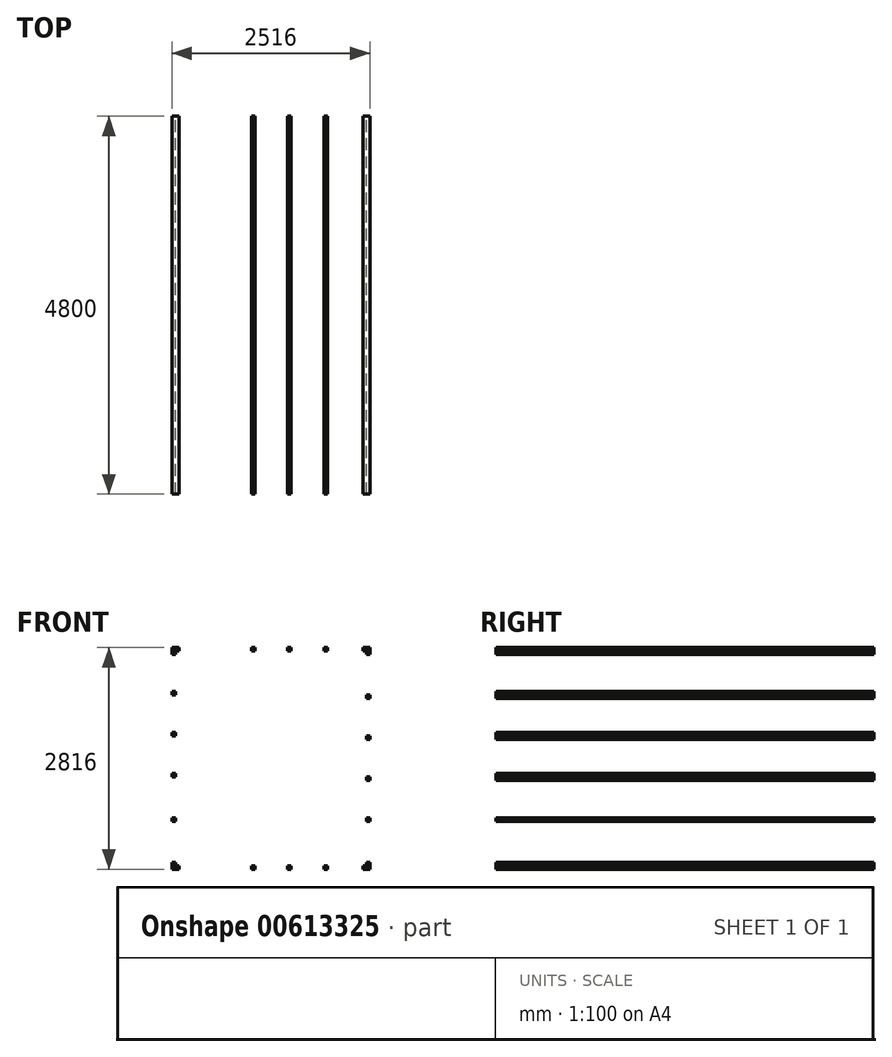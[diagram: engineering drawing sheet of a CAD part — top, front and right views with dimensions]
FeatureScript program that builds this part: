
annotation { "Feature Type Name" : "Feature", "Feature Type Description" : "" }
export const myFeature = defineFeature(function(context is Context, id is Id, definition is map)
    precondition{}
    {
        {
            var Q0;
            Q0=qCreatedBy(makeId("Front.planeOp"),FACE);
            var sketch = newSketch(context, id + "F0", { "sketchPlane" : qUnion([Q0])});
            skLineSegment(sketch, "E0.bottom", {"start": v(0, 0) * mm, "end": v(2400, 0) * mm});
            skLineSegment(sketch, "E0.top", {"start": v(0, 2700) * mm, "end": v(2400, 2700) * mm});
            skLineSegment(sketch, "E0.left", {"start": v(0, 0) * mm, "end": v(0, 2700) * mm});
            skLineSegment(sketch, "E0.right", {"start": v(2400, 0) * mm, "end": v(2400, 2700) * mm});
            skLineSegment(sketch, "E1.0", {"start": v(145, 2555) * mm, "end": v(2255, 2555) * mm});
            skLineSegment(sketch, "E1.1", {"start": v(145, 145) * mm, "end": v(145, 2555) * mm});
            skLineSegment(sketch, "E1.2", {"start": v(145, 145) * mm, "end": v(2255, 145) * mm});
            skLineSegment(sketch, "E1.3", {"start": v(2255, 145) * mm, "end": v(2255, 2555) * mm});
            skLineSegment(sketch, "E2.0", {"start": v(-13, 2713) * mm, "end": v(2413, 2713) * mm});
            skLineSegment(sketch, "E2.1", {"start": v(-13, -13) * mm, "end": v(-13, 2713) * mm});
            skLineSegment(sketch, "E2.2", {"start": v(-13, -13) * mm, "end": v(2413, -13) * mm});
            skLineSegment(sketch, "E2.3", {"start": v(2413, -13) * mm, "end": v(2413, 2713) * mm});
            skLineSegment(sketch, "E3.bottom", {"start": v(-13, 2713) * mm, "end": v(-58, 2713) * mm});
            skLineSegment(sketch, "E3.top", {"start": v(-13, 2668) * mm, "end": v(-58, 2668) * mm});
            skLineSegment(sketch, "E3.left", {"start": v(-13, 2713) * mm, "end": v(-13, 2668) * mm});
            skLineSegment(sketch, "E3.right", {"start": v(-58, 2713) * mm, "end": v(-58, 2668) * mm});
            skLineSegment(sketch, "E4.bottom", {"start": v(2413, 2713) * mm, "end": v(2458, 2713) * mm});
            skLineSegment(sketch, "E4.top", {"start": v(2413, 2668) * mm, "end": v(2458, 2668) * mm});
            skLineSegment(sketch, "E4.left", {"start": v(2413, 2713) * mm, "end": v(2413, 2668) * mm});
            skLineSegment(sketch, "E4.right", {"start": v(2458, 2713) * mm, "end": v(2458, 2668) * mm});
            skLineSegment(sketch, "E5.bottom", {"start": v(-13, -13) * mm, "end": v(-58, -13) * mm});
            skLineSegment(sketch, "E5.top", {"start": v(-13, 32) * mm, "end": v(-58, 32) * mm});
            skLineSegment(sketch, "E5.left", {"start": v(-13, -13) * mm, "end": v(-13, 32) * mm});
            skLineSegment(sketch, "E5.right", {"start": v(-58, -13) * mm, "end": v(-58, 32) * mm});
            skLineSegment(sketch, "E6.bottom", {"start": v(2413, -13) * mm, "end": v(2458, -13) * mm});
            skLineSegment(sketch, "E6.top", {"start": v(2413, 32) * mm, "end": v(2458, 32) * mm});
            skLineSegment(sketch, "E6.left", {"start": v(2413, -13) * mm, "end": v(2413, 32) * mm});
            skLineSegment(sketch, "E6.right", {"start": v(2458, -13) * mm, "end": v(2458, 32) * mm});
            skLineSegment(sketch, "E7.bottom", {"start": v(-58, 2713) * mm, "end": v(32, 2713) * mm});
            skLineSegment(sketch, "E7.top", {"start": v(-58, 2758) * mm, "end": v(32, 2758) * mm});
            skLineSegment(sketch, "E7.left", {"start": v(-58, 2713) * mm, "end": v(-58, 2758) * mm});
            skLineSegment(sketch, "E7.right", {"start": v(32, 2713) * mm, "end": v(32, 2758) * mm});
            skLineSegment(sketch, "E8.bottom", {"start": v(-58, -13) * mm, "end": v(32, -13) * mm});
            skLineSegment(sketch, "E8.top", {"start": v(-58, -58) * mm, "end": v(32, -58) * mm});
            skLineSegment(sketch, "E8.left", {"start": v(-58, -13) * mm, "end": v(-58, -58) * mm});
            skLineSegment(sketch, "E8.right", {"start": v(32, -13) * mm, "end": v(32, -58) * mm});
            skLineSegment(sketch, "E9.bottom", {"start": v(2458, -13) * mm, "end": v(2368, -13) * mm});
            skLineSegment(sketch, "E9.top", {"start": v(2458, -58) * mm, "end": v(2368, -58) * mm});
            skLineSegment(sketch, "E9.left", {"start": v(2458, -13) * mm, "end": v(2458, -58) * mm});
            skLineSegment(sketch, "E9.right", {"start": v(2368, -13) * mm, "end": v(2368, -58) * mm});
            skLineSegment(sketch, "E10.bottom", {"start": v(2458, 2713) * mm, "end": v(2368, 2713) * mm});
            skLineSegment(sketch, "E10.top", {"start": v(2458, 2758) * mm, "end": v(2368, 2758) * mm});
            skLineSegment(sketch, "E10.left", {"start": v(2458, 2713) * mm, "end": v(2458, 2758) * mm});
            skLineSegment(sketch, "E10.right", {"start": v(2368, 2713) * mm, "end": v(2368, 2758) * mm});
            skLineSegment(sketch, "E11.bottom", {"start": v(492, 2713) * mm, "end": v(537, 2713) * mm});
            skLineSegment(sketch, "E11.top", {"start": v(492, 2758) * mm, "end": v(537, 2758) * mm});
            skLineSegment(sketch, "E11.left", {"start": v(492, 2713) * mm, "end": v(492, 2758) * mm});
            skLineSegment(sketch, "E11.right", {"start": v(537, 2713) * mm, "end": v(537, 2758) * mm});
            skLineSegment(sketch, "E12.1.0.0", {"start": v(952, 2713) * mm, "end": v(952, 2758) * mm});
            skLineSegment(sketch, "E12.1.0.1", {"start": v(952, 2758) * mm, "end": v(997, 2758) * mm});
            skLineSegment(sketch, "E12.1.0.2", {"start": v(997, 2713) * mm, "end": v(997, 2758) * mm});
            skLineSegment(sketch, "E12.2.0.0", {"start": v(1412, 2713) * mm, "end": v(1412, 2758) * mm});
            skLineSegment(sketch, "E12.2.0.1", {"start": v(1412, 2758) * mm, "end": v(1457, 2758) * mm});
            skLineSegment(sketch, "E12.2.0.2", {"start": v(1457, 2713) * mm, "end": v(1457, 2758) * mm});
            skLineSegment(sketch, "E12.3.0.0", {"start": v(1872, 2713) * mm, "end": v(1872, 2758) * mm});
            skLineSegment(sketch, "E12.3.0.1", {"start": v(1872, 2758) * mm, "end": v(1917, 2758) * mm});
            skLineSegment(sketch, "E12.3.0.2", {"start": v(1917, 2713) * mm, "end": v(1917, 2758) * mm});
            skLineSegment(sketch, "E12.direction1", {"start": v(492, 2713) * mm, "end": v(952, 2713) * mm, "construction": true});
            skLineSegment(sketch, "E13.bottom", {"start": v(492, -13) * mm, "end": v(537, -13) * mm});
            skLineSegment(sketch, "E13.top", {"start": v(492, -58) * mm, "end": v(537, -58) * mm});
            skLineSegment(sketch, "E13.left", {"start": v(492, -13) * mm, "end": v(492, -58) * mm});
            skLineSegment(sketch, "E13.right", {"start": v(537, -13) * mm, "end": v(537, -58) * mm});
            skLineSegment(sketch, "E14.1.0.0", {"start": v(952, -13) * mm, "end": v(952, -58) * mm});
            skLineSegment(sketch, "E14.1.0.1", {"start": v(952, -58) * mm, "end": v(997, -58) * mm});
            skLineSegment(sketch, "E14.1.0.2", {"start": v(997, -13) * mm, "end": v(997, -58) * mm});
            skLineSegment(sketch, "E14.2.0.0", {"start": v(1412, -13) * mm, "end": v(1412, -58) * mm});
            skLineSegment(sketch, "E14.2.0.1", {"start": v(1412, -58) * mm, "end": v(1457, -58) * mm});
            skLineSegment(sketch, "E14.2.0.2", {"start": v(1457, -13) * mm, "end": v(1457, -58) * mm});
            skLineSegment(sketch, "E14.3.0.0", {"start": v(1872, -13) * mm, "end": v(1872, -58) * mm});
            skLineSegment(sketch, "E14.3.0.1", {"start": v(1872, -58) * mm, "end": v(1917, -58) * mm});
            skLineSegment(sketch, "E14.3.0.2", {"start": v(1917, -13) * mm, "end": v(1917, -58) * mm});
            skLineSegment(sketch, "E14.direction1", {"start": v(492, -58) * mm, "end": v(952, -58) * mm, "construction": true});
            skLineSegment(sketch, "E15.bottom", {"start": v(-13, 597) * mm, "end": v(-58, 597) * mm});
            skLineSegment(sketch, "E15.top", {"start": v(-13, 552) * mm, "end": v(-58, 552) * mm});
            skLineSegment(sketch, "E15.left", {"start": v(-13, 597) * mm, "end": v(-13, 552) * mm});
            skLineSegment(sketch, "E15.right", {"start": v(-58, 597) * mm, "end": v(-58, 552) * mm});
            skLineSegment(sketch, "E16.bottom", {"start": v(2413, 597) * mm, "end": v(2458, 597) * mm});
            skLineSegment(sketch, "E16.top", {"start": v(2413, 552) * mm, "end": v(2458, 552) * mm});
            skLineSegment(sketch, "E16.left", {"start": v(2413, 597) * mm, "end": v(2413, 552) * mm});
            skLineSegment(sketch, "E16.right", {"start": v(2458, 597) * mm, "end": v(2458, 552) * mm});
            skLineSegment(sketch, "E17.0.1.0", {"start": v(2413, 1117) * mm, "end": v(2458, 1117) * mm});
            skLineSegment(sketch, "E17.0.1.1", {"start": v(2413, 1072) * mm, "end": v(2458, 1072) * mm});
            skLineSegment(sketch, "E17.0.1.2", {"start": v(2458, 1117) * mm, "end": v(2458, 1072) * mm});
            skLineSegment(sketch, "E17.0.2.0", {"start": v(2413, 1637) * mm, "end": v(2458, 1637) * mm});
            skLineSegment(sketch, "E17.0.2.1", {"start": v(2413, 1592) * mm, "end": v(2458, 1592) * mm});
            skLineSegment(sketch, "E17.0.2.2", {"start": v(2458, 1637) * mm, "end": v(2458, 1592) * mm});
            skLineSegment(sketch, "E17.0.3.0", {"start": v(2413, 2157) * mm, "end": v(2458, 2157) * mm});
            skLineSegment(sketch, "E17.0.3.1", {"start": v(2413, 2112) * mm, "end": v(2458, 2112) * mm});
            skLineSegment(sketch, "E17.0.3.2", {"start": v(2458, 2157) * mm, "end": v(2458, 2112) * mm});
            skLineSegment(sketch, "E17.direction1", {"start": v(2413, 552) * mm, "end": v(2438, 552) * mm, "construction": true});
            skLineSegment(sketch, "E17.direction2", {"start": v(2413, 552) * mm, "end": v(2413, 1072) * mm, "construction": true});
            skLineSegment(sketch, "E18.bottom", {"start": v(-13, 1117) * mm, "end": v(-58, 1117) * mm});
            skLineSegment(sketch, "E18.top", {"start": v(-13, 1162) * mm, "end": v(-58, 1162) * mm});
            skLineSegment(sketch, "E18.left", {"start": v(-13, 1117) * mm, "end": v(-13, 1162) * mm});
            skLineSegment(sketch, "E18.right", {"start": v(-58, 1117) * mm, "end": v(-58, 1162) * mm});
            skLineSegment(sketch, "E19.0.1.0", {"start": v(-13, 1682) * mm, "end": v(-58, 1682) * mm});
            skLineSegment(sketch, "E19.0.1.1", {"start": v(-58, 1637) * mm, "end": v(-58, 1682) * mm});
            skLineSegment(sketch, "E19.0.1.2", {"start": v(-13, 1637) * mm, "end": v(-58, 1637) * mm});
            skLineSegment(sketch, "E19.0.2.0", {"start": v(-13, 2202) * mm, "end": v(-58, 2202) * mm});
            skLineSegment(sketch, "E19.0.2.1", {"start": v(-58, 2157) * mm, "end": v(-58, 2202) * mm});
            skLineSegment(sketch, "E19.0.2.2", {"start": v(-13, 2157) * mm, "end": v(-58, 2157) * mm});
            skLineSegment(sketch, "E19.direction1", {"start": v(-58, 1117) * mm, "end": v(-33, 1117) * mm, "construction": true});
            skLineSegment(sketch, "E19.direction2", {"start": v(-58, 1117) * mm, "end": v(-58, 1637) * mm, "construction": true});
            skLineSegment(sketch, "E20.0", {"start": v(-58, 2758) * mm, "end": v(2458, 2758) * mm});
            skLineSegment(sketch, "E20.1", {"start": v(-58, -58) * mm, "end": v(-58, 2758) * mm});
            skLineSegment(sketch, "E20.2", {"start": v(-58, -58) * mm, "end": v(2458, -58) * mm});
            skLineSegment(sketch, "E20.3", {"start": v(2458, -58) * mm, "end": v(2458, 2758) * mm});
            skSolve(sketch);
        }
        {
            var Q0;
            Q0=makeQuery(id+"F0.imprint","IMPRINT",FACE,{"disambiguationData":[TD([[makeQuery(id+"F0.imprint","IMPRINT",EDGE,{"derivedFrom":sQuery(id+"F0.wireOp",EDGE,"E7.top")}),-1.0]])]});
            var Q1;
            Q1=makeQuery(id+"F0.imprint","IMPRINT",FACE,{"disambiguationData":[TD([[makeQuery(id+"F0.imprint","IMPRINT",EDGE,{"derivedFrom":sQuery(id+"F0.wireOp",EDGE,"E10.top")}),1.0]])]});
            var Q2;
            Q2=makeQuery(id+"F0.imprint","IMPRINT",FACE,{"disambiguationData":[TD([[makeQuery(id+"F0.imprint","IMPRINT",EDGE,{"derivedFrom":sQuery(id+"F0.wireOp",EDGE,"E8.top")}),1.0]])]});
            var Q3;
            Q3=makeQuery(id+"F0.imprint","IMPRINT",FACE,{"disambiguationData":[TD([[makeQuery(id+"F0.imprint","IMPRINT",EDGE,{"derivedFrom":sQuery(id+"F0.wireOp",EDGE,"E9.top")}),-1.0]])]});
            extrude(context, id + "F1", {"entities" : qUnion([Q0, Q1, Q2, Q3]), "depth" : 4800 * mm, "offsetDistance" : 25 * mm});
        }
        {
            var Q0;
            Q0=makeQuery(id+"F0.imprint","IMPRINT",FACE,{"disambiguationData":[TD([[makeQuery(id+"F0.imprint","IMPRINT",EDGE,{"derivedFrom":sQuery(id+"F0.wireOp",EDGE,"E3.top")}),-1.0]])]});
            var Q1;
            Q1=makeQuery(id+"F0.imprint","IMPRINT",FACE,{"disambiguationData":[TD([[makeQuery(id+"F0.imprint","IMPRINT",EDGE,{"derivedFrom":sQuery(id+"F0.wireOp",EDGE,"E4.top")}),1.0]])]});
            var Q2;
            Q2=makeQuery(id+"F0.imprint","IMPRINT",FACE,{"disambiguationData":[TD([[makeQuery(id+"F0.imprint","IMPRINT",EDGE,{"derivedFrom":sQuery(id+"F0.wireOp",EDGE,"E11.bottom")}),1.0]])]});
            var Q3;
            {var subQ0=sQuery(id+"F0.wireOp",EDGE,"E12.1.0.0");Q3=makeQuery(id+"F0.imprint","IMPRINT",FACE,{"disambiguationData":[TD([[makeQuery(id+"F0.imprint","IMPRINT",EDGE,{"derivedFrom":subQ0}),-1.0]])]});}
            var Q4;
            {var subQ0=sQuery(id+"F0.wireOp",EDGE,"E12.2.0.0");Q4=makeQuery(id+"F0.imprint","IMPRINT",FACE,{"disambiguationData":[TD([[makeQuery(id+"F0.imprint","IMPRINT",EDGE,{"derivedFrom":subQ0}),-1.0]])]});}
            var Q5;
            {var subQ0=sQuery(id+"F0.wireOp",EDGE,"E12.3.0.0");Q5=makeQuery(id+"F0.imprint","IMPRINT",FACE,{"disambiguationData":[TD([[makeQuery(id+"F0.imprint","IMPRINT",EDGE,{"derivedFrom":subQ0}),-1.0]])]});}
            var Q6;
            {var subQ0=sQuery(id+"F0.wireOp",EDGE,"E19.0.2.0");Q6=makeQuery(id+"F0.imprint","IMPRINT",FACE,{"disambiguationData":[TD([[makeQuery(id+"F0.imprint","IMPRINT",EDGE,{"derivedFrom":subQ0}),1.0]])]});}
            var Q7;
            {var subQ0=sQuery(id+"F0.wireOp",EDGE,"E19.0.1.0");Q7=makeQuery(id+"F0.imprint","IMPRINT",FACE,{"disambiguationData":[TD([[makeQuery(id+"F0.imprint","IMPRINT",EDGE,{"derivedFrom":subQ0}),1.0]])]});}
            var Q8;
            Q8=makeQuery(id+"F0.imprint","IMPRINT",FACE,{"disambiguationData":[TD([[makeQuery(id+"F0.imprint","IMPRINT",EDGE,{"derivedFrom":sQuery(id+"F0.wireOp",EDGE,"E18.bottom")}),-1.0]])]});
            var Q9;
            Q9=makeQuery(id+"F0.imprint","IMPRINT",FACE,{"disambiguationData":[TD([[makeQuery(id+"F0.imprint","IMPRINT",EDGE,{"derivedFrom":sQuery(id+"F0.wireOp",EDGE,"E15.bottom")}),1.0]])]});
            var Q10;
            Q10=makeQuery(id+"F0.imprint","IMPRINT",FACE,{"disambiguationData":[TD([[makeQuery(id+"F0.imprint","IMPRINT",EDGE,{"derivedFrom":sQuery(id+"F0.wireOp",EDGE,"E5.top")}),1.0]])]});
            var Q11;
            Q11=makeQuery(id+"F0.imprint","IMPRINT",FACE,{"disambiguationData":[TD([[makeQuery(id+"F0.imprint","IMPRINT",EDGE,{"derivedFrom":sQuery(id+"F0.wireOp",EDGE,"E6.top")}),-1.0]])]});
            var Q12;
            Q12=makeQuery(id+"F0.imprint","IMPRINT",FACE,{"disambiguationData":[TD([[makeQuery(id+"F0.imprint","IMPRINT",EDGE,{"derivedFrom":sQuery(id+"F0.wireOp",EDGE,"E16.bottom")}),-1.0]])]});
            var Q13;
            {var subQ0=sQuery(id+"F0.wireOp",EDGE,"E17.0.1.0");Q13=makeQuery(id+"F0.imprint","IMPRINT",FACE,{"disambiguationData":[TD([[makeQuery(id+"F0.imprint","IMPRINT",EDGE,{"derivedFrom":subQ0}),-1.0]])]});}
            var Q14;
            {var subQ0=sQuery(id+"F0.wireOp",EDGE,"E17.0.2.0");Q14=makeQuery(id+"F0.imprint","IMPRINT",FACE,{"disambiguationData":[TD([[makeQuery(id+"F0.imprint","IMPRINT",EDGE,{"derivedFrom":subQ0}),-1.0]])]});}
            var Q15;
            {var subQ0=sQuery(id+"F0.wireOp",EDGE,"E17.0.3.0");Q15=makeQuery(id+"F0.imprint","IMPRINT",FACE,{"disambiguationData":[TD([[makeQuery(id+"F0.imprint","IMPRINT",EDGE,{"derivedFrom":subQ0}),-1.0]])]});}
            var Q16;
            Q16=makeQuery(id+"F0.imprint","IMPRINT",FACE,{"disambiguationData":[TD([[makeQuery(id+"F0.imprint","IMPRINT",EDGE,{"derivedFrom":sQuery(id+"F0.wireOp",EDGE,"E13.bottom")}),-1.0]])]});
            var Q17;
            {var subQ0=sQuery(id+"F0.wireOp",EDGE,"E14.1.0.0");Q17=makeQuery(id+"F0.imprint","IMPRINT",FACE,{"disambiguationData":[TD([[makeQuery(id+"F0.imprint","IMPRINT",EDGE,{"derivedFrom":subQ0}),1.0]])]});}
            var Q18;
            {var subQ0=sQuery(id+"F0.wireOp",EDGE,"E14.2.0.0");Q18=makeQuery(id+"F0.imprint","IMPRINT",FACE,{"disambiguationData":[TD([[makeQuery(id+"F0.imprint","IMPRINT",EDGE,{"derivedFrom":subQ0}),1.0]])]});}
            var Q19;
            {var subQ0=sQuery(id+"F0.wireOp",EDGE,"E14.3.0.0");Q19=makeQuery(id+"F0.imprint","IMPRINT",FACE,{"disambiguationData":[TD([[makeQuery(id+"F0.imprint","IMPRINT",EDGE,{"derivedFrom":subQ0}),1.0]])]});}
            extrude(context, id + "F2", {"entities" : qUnion([Q0, Q1, Q2, Q3, Q4, Q5, Q6, Q7, Q8, Q9, Q10, Q11, Q12, Q13, Q14, Q15, Q16, Q17, Q18, Q19]), "depth" : 4800 * mm, "offsetDistance" : 25 * mm});
        }
    });
